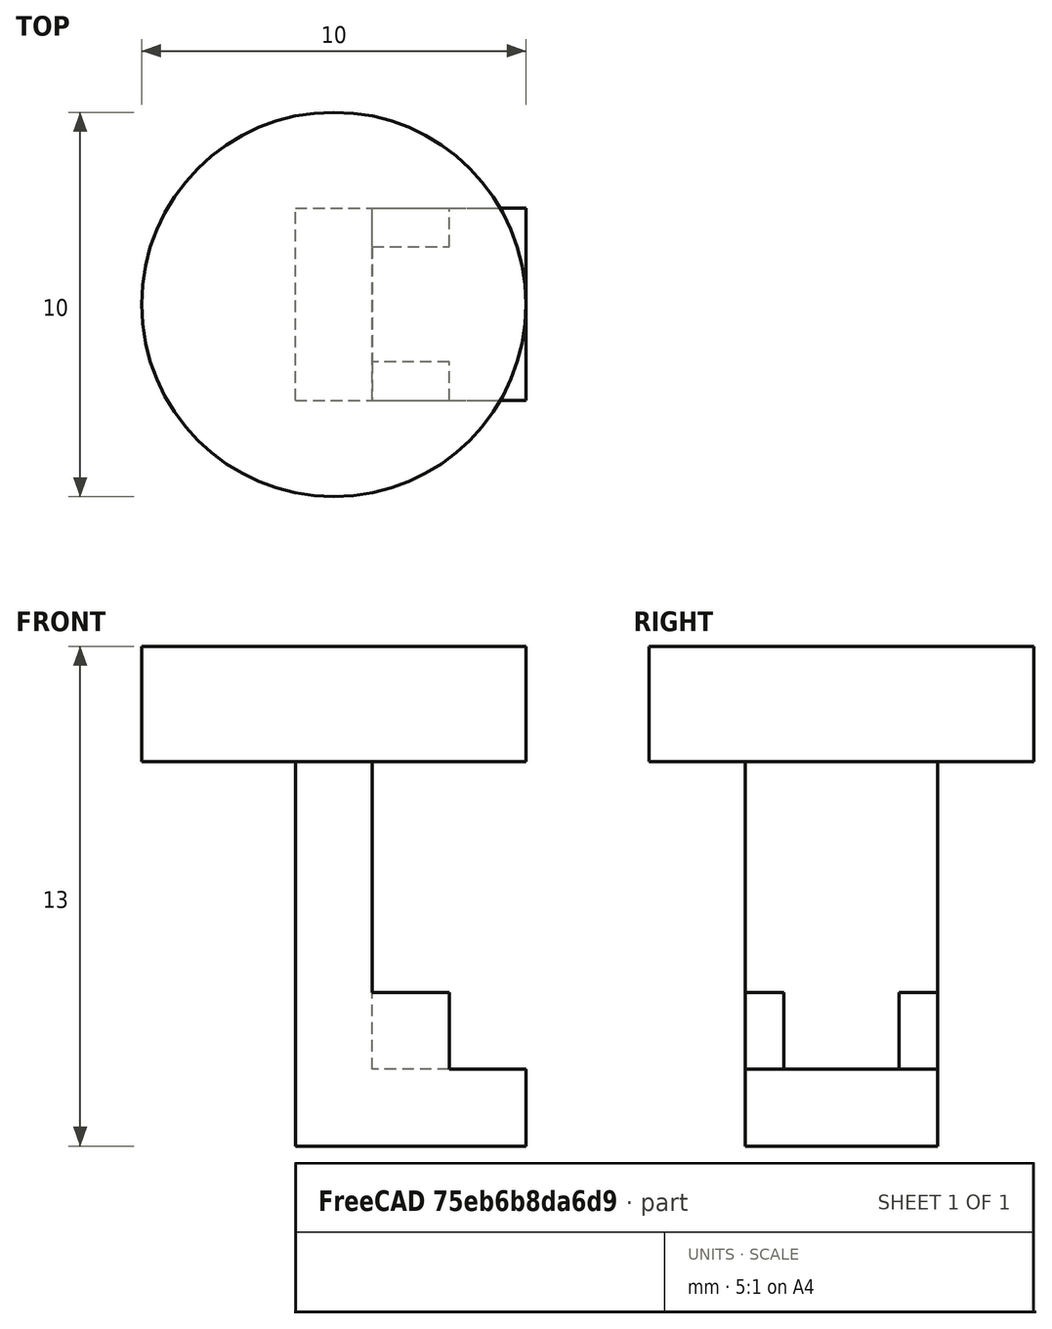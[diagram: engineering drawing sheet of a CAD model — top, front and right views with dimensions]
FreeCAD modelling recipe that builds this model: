
FCSTD DOCUMENT  (FreeCAD 0.17R11508 (Git))
Label: torquetest
License: All rights reserved
LicenseURL: http://en.wikipedia.org/wiki/All_rights_reserved
objects: Part::Box×4, App::MaterialObjectPython×2, Fem::FemMeshObjectPython×2, Fem::FemSolverObjectPython×1, Sketcher::SketchObject×1, Part::Extrusion×1, Part::MultiFuse×1, Part::FeaturePython×1, Fem::ConstraintFixed×1, Fem::ConstraintDisplacement×1, Fem::ConstraintTransform×1, Fem::FemResultObjectPython×1, Fem::FemAnalysisPython×1
note: 8 computed .brp shape members not serialized (recipe doc carries the construction recipe); baked Part::Feature solids carry a one-line shape summary decoded from their .brp

FEATURE [Part::Box] Box  label="Cube"
  AttacherType = Attacher::AttachEngine3D
  Height = 10
  Length = 2
  Width = 5
FEATURE [Part::Box] Box001  label="Cube001"
  AttacherType = Attacher::AttachEngine3D
  Height = 2
  Length = 6
  Width = 5
FEATURE [Part::Box] Box002  label="Cube002"
  AttacherType = Attacher::AttachEngine3D
  Height = 4
  Length = 4
  Width = 1
FEATURE [Part::Box] Box003  label="Cube003"
  AttacherType = Attacher::AttachEngine3D
  Height = 4
  Length = 4
  Placement = pos=(0,4,0) rot=(0,0,1;0rad)
  Width = 1
FEATURE [Fem::FemSolverObjectPython] CalculiX  # FEM object (typed FeaturePython)
  AnalysisType = 0
  EigenmodeHighLimit = 1000000
  EigenmodeLowLimit = 0
  EigenmodesCount = 10
  GeometricalNonlinearity = 0
  IterationsControlParameterCutb = 0.25,0.5,0.75,0.85,,,1.5,
  IterationsControlParameterIter = 4,8,9,200,10,400,,200,,
  IterationsControlParameterTimeUse = false
  IterationsThermoMechMaximum = 2000
  IterationsUserDefinedIncrementations = false
  IterationsUserDefinedTimeStepLength = false
  MaterialNonlinearity = 0
  MatrixSolverType = 0
  SolverType = FemSolverCalculix
  SplitInputWriter = false
  ThermoMechSteadyState = true
  TimeEnd = 1
  TimeInitialStep = 0.01
FEATURE [App::MaterialObjectPython] SolidMaterial  # material (typed FeaturePython)
  Category = 0
  Material = Density=1300.0 kg/m^3,+11 more (map truncated)
FEATURE [Sketcher::SketchObject] Sketch
  ExternalGeometry = -> [Box]
  MapMode = 5
  Placement = pos=(0,0,10) rot=(0,0,1;0rad)
  Support = -> [Box]
  sketch-geometry (1):
    g0: Circle CenterX=1 CenterY=2.5 CenterZ=0 NormalX=0 NormalY=0 NormalZ=1 Radius=5
  constraints (5):
    c: Radius(g0) = 5
    c: DistanceX(g-1,g0) = 1
    c: DistanceX(g-4,g-3) = 2
    c: DistanceY(g-3,g-3) = 5
    c: DistanceY(g-1,g0) = 2.5
FEATURE [Part::Extrusion] Extrude
  Base = -> Sketch
  Dir = (0,0,1)
  DirMode = 2
  FaceMakerClass = Part::FaceMakerBullseye
  LengthFwd = 3
  LengthRev = 0
  Solid = true
  Symmetric = false
FEATURE [Fem::FemMeshObjectPython] FEMMeshGMSH  # FEM object (typed FeaturePython)
  Algorithm2D = 0
  Algorithm3D = 0
  CharacteristicLengthMax = 0
  CharacteristicLengthMin = 0
  CoherenceMesh = true
  ElementDimension = 0
  ElementOrder = 1
  GeometryTolerance = 1e-06
  HighOrderOptimize = false
  OptimizeNetgen = false
  OptimizeStd = true
  RecombineAll = false
FEATURE [Part::MultiFuse] Fusion
  Shapes = -> [Box003,Box,Box001,Box002]
FEATURE [Part::FeaturePython] BooleanFragments  # WARN: FeaturePython — macro-defined, semantics opaque (R4)
  Mode = 0
  Objects = -> [Fusion,Extrude]
  Tolerance = 0
FEATURE [Fem::ConstraintFixed] FemConstraintFixed
  NormalDirection = (0,0,-1)
  Normals = (9) [(0,0,-1),(0,0,-1),(0,0,-1),(0,0,-1),(0,0,-1),(0,0,-1),(0,0,-1),(0,0,-1),(0,0,-1)]
  Points = (9) [(0,0,0),(3,0,0),(6,0,0),(0,2.5,0),(3,2.5,0),(6,2.5,0),(0,5,0),(3,5,0),(6,5,0)]
  References = -> [BooleanFragments]
FEATURE [Fem::ConstraintDisplacement] FemConstraintDisplacement
  NormalDirection = (-1,0,0)
  Normals = (12) [(1,0,0),(-0.5,0.866025,0),(-0.5,-0.866025,0),(1,-2.44929e-16,0),(1,0,0),(-0.5,0.866025,0),(-0.5,-0.866025,0),(1,-2.44929e-16,0),(1,0,0),+3 more]
  Points = (12) [(6,2.5,13),(-1.5,6.83013,13),(-1.5,-1.83013,13),(6,2.5,13),(6,2.5,11.5),(-1.5,6.83013,11.5),(-1.5,-1.83013,11.5),(6,2.5,11.5),(6,2.5,10),+3 more]
  References = -> [BooleanFragments]
  Scale = 2
  rotxFix = false
  rotxFree = true
  rotyFix = false
  rotyFree = true
  rotzFix = false
  rotzFree = true
  xDisplacement = 0
  xFix = false
  xFree = true
  xRotation = 0
  yDisplacement = 0.01
  yFix = false
  yFree = false
  yRotation = 0
  zDisplacement = 0
  zFix = false
  zFree = true
  zRotation = 0
FEATURE [Fem::ConstraintTransform] FemConstraintTransform
  Axis = (0,0,-1)
  BasePoint = (1,2.5,8.5)
  NameDispl = -> [FemConstraintDisplacement]
  NormalDirection = (-1,0,0)
  Normals = (12) [(1,0,0),(-0.5,0.866025,0),(-0.5,-0.866025,0),(1,-2.44929e-16,0),(1,0,0),(-0.5,0.866025,0),(-0.5,-0.866025,0),(1,-2.44929e-16,0),(1,0,0),+3 more]
  Points = (12) [(6,2.5,13),(-1.5,6.83013,13),(-1.5,-1.83013,13),(6,2.5,13),(6,2.5,11.5),(-1.5,6.83013,11.5),(-1.5,-1.83013,11.5),(6,2.5,11.5),(6,2.5,10),+3 more]
  RefDispl = -> [BooleanFragments]
  References = -> [BooleanFragments]
  Scale = 2
  TransformType = 0
  X_rot = 0
  Y_rot = 0
  Z_rot = 0
FEATURE [App::MaterialObjectPython] SolidMaterial001  # material (typed FeaturePython)
  Category = 0
  Material = Density=7900.0 kg/m^3,Description=Standard steel material for CalculiX sample calculations,Father=Metal,Name=CalculiX-Steel,PoissonRatio=0.3,+4 more (map truncated)
  References = -> [BooleanFragments]
FEATURE [Fem::FemMeshObjectPython] Result_mesh  # FEM object (typed FeaturePython)
FEATURE [Fem::FemResultObjectPython] CalculiX_static_results  # FEM object (typed FeaturePython)
  DisplacementLengths = [0.01,0.01,0.00538327,0.00538318,0.00538338,0.00538346,0.000866483,0.000864601,0.000729241,0.000158281,0.000158271,0.000732636,0.000654506,0.00070163,0.000137894,0.000169863,0.00010002,0.000102148,0.000170368,0.000139083,0.000703469,+1725 more]
  DisplacementVectors = (1746) [(2.20489e-09,0.01,2.86432e-07),(1.26232e-08,0.01,2.89137e-07),(-0.00499778,0.00200044,1.90102e-06),(-0.00499779,-0.00200017,-1.52086e-06),+1742 more]
  Eigenmode = 0
  EigenmodeFrequency = 0
  MaxShear = [0.0524846,0.0459467,0.294052,0.303209,0.332407,0.259663,0.901298,0.901346,0.402966,0.162882,0.159979,0.405364,0.0349668,0.0387366,0.33963,0.267905,0.0210362,0.021571,0.268696,0.339734,0.0388228,0.034943,0.0932425,0.0933804,0.143642,+1721 more]
  Mesh = -> FEMMeshGMSH
  NodeNumbers = [1,2,3,4,5,6,7,8,9,10,11,12,13,14,15,16,17,18,19,20,21,22,23,24,25,26,27,28,29,30,31,32,33,34,35,36,37,38,39,40,41,42,43,44,45,46,47,48,49,50,51,52,53,54,55,56,57,58,59,60,61,62,63,64,65,66,67,68,69,+1677 more]
  PrincipalMax = [0.0523492,0.0507218,-0.0796789,0.681522,-0.0644553,0.583525,0.265298,1.53898,0.682912,0.272676,0.0535128,0.125722,0.0241069,0.0290042,0.742203,0.48779,0.0139028,0.0299096,0.0483014,-0.0643289,0.0485862,0.0457182,0.00398749,0.183917,+1722 more]
  PrincipalMed = [6.8002e-05,0.00314552,-0.320404,0.339239,-0.356962,0.270717,-1.21429,1.21543,0.0688701,0.0489608,-0.0521777,-0.0777548,-0.0272732,-0.0306289,0.330756,0.37282,-0.0118869,0.0152755,-0.37303,-0.331016,0.0307064,0.0272082,-0.0547449,0.0554244,+1722 more]
  PrincipalMin = [-0.0526201,-0.0411715,-0.667783,0.0751035,-0.72927,0.0641992,-1.5373,-0.263709,-0.12302,-0.0530884,-0.266445,-0.685005,-0.0458267,-0.048469,0.062943,-0.0480212,-0.0281695,-0.0132325,-0.489091,-0.743797,-0.0290594,-0.0241679,-0.182498,+1723 more]
  ResultType = FemResultMechanical
  Stats = [-0.0099742,-8.5185e-05,0.00999882,-0.01,0.000167154,0.01,-0.000471814,4.89687e-07,0.000470526,0,0.00348165,0.01,0.0103325,0.288642,1.66476,-0.245484,0.163018,1.53898,-1.21429,-0.000336906,1.21543,-1.5373,-0.163331,0.257947,0.00595263,+5 more]
  StrainVectors = (1746) [(7.97989e-11,6.28903e-11,-5.29265e-10),(4.37718e-09,2.90898e-08,-9.28444e-09),(8.27912e-06,1.00889e-05,-6.51738e-05),+1743 more]
  StressValues = [0.0909063,0.0795986,0.512097,0.526625,0.577127,0.452878,1.66476,1.66467,0.729176,0.288604,0.28236,0.73056,0.062749,0.0702726,0.592625,0.488579,0.0367445,0.0380006,0.489786,0.592953,0.070429,0.0627144,0.165147,0.165507,0.260133,0.260381,+1720 more]
  StressVectors = (1746) [(-3.39446e-05,-3.6676e-05,-0.000132332),(0.00363689,0.00762893,0.00143001),(-0.339255,-0.187871,-0.54074),(0.350666,0.19142,0.553778),+1742 more]
  Time = 0
FEATURE [Fem::FemAnalysisPython] Analysis  # FEM object (typed FeaturePython)
  Member = -> [CalculiX,SolidMaterial,FemConstraintFixed,FemConstraintDisplacement,FemConstraintTransform,FEMMeshGMSH,SolidMaterial001,CalculiX_static_results,Result_mesh]
